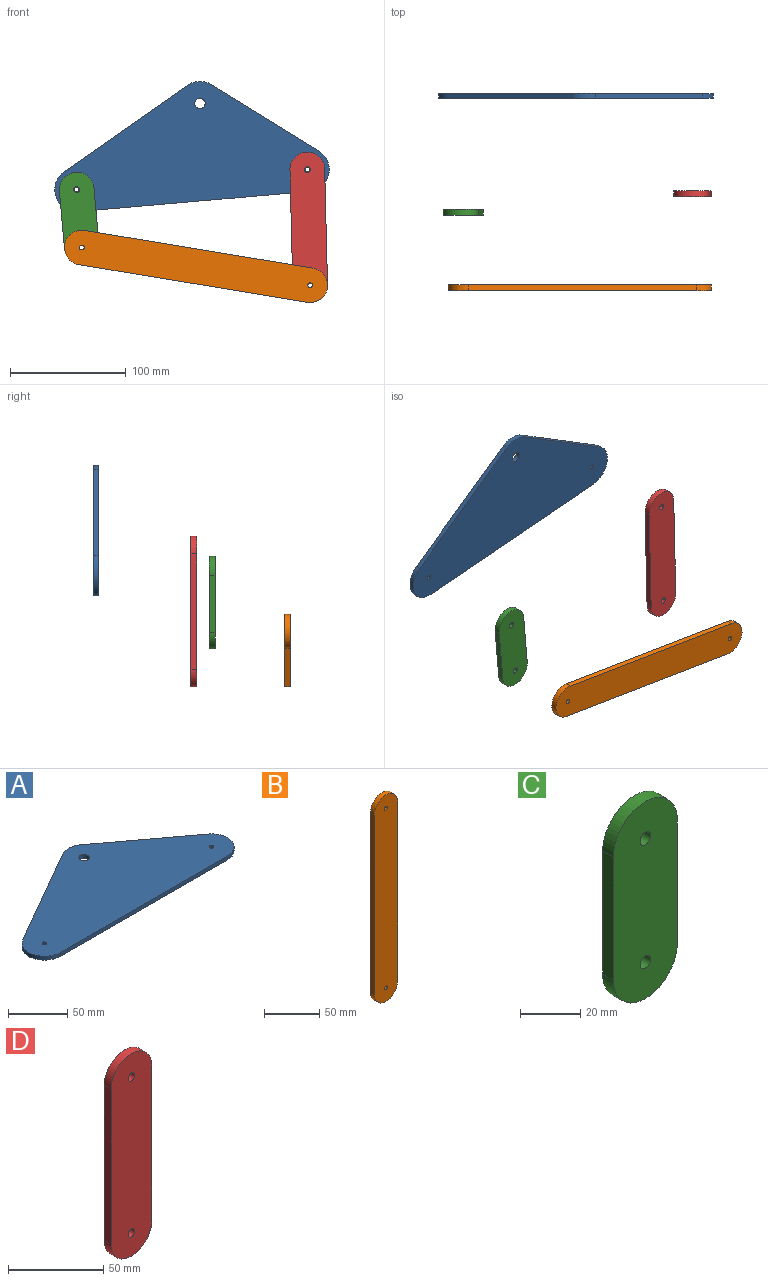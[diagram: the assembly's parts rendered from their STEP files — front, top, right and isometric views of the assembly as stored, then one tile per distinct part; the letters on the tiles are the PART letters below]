
ASSEMBLY  parts=4 mates=4
PART A: 11 faces, bbox 238x103x4 mm
  f0: plane 112.58x65mm, normal (-0.5,0.87,0), area 520mm2, adj f1,f8,f9,f10
  f1: cylinder r=19mm len=35.45mm, axis (0,0,-1), area 199mm2, adj f0,f2,f9,f10
  f2: plane 200x4mm, normal (0,-1,0), area 800mm2, adj f1,f3,f9,f10
  f3: cylinder r=19mm len=34.25mm, axis (0,0,-1), area 190.2mm2, adj f2,f4,f9,f10
  f4: plane 87.42x65mm, normal (0.6,0.8,0), area 435.7mm2, adj f3,f8,f9,f10
  f5: cylinder r=2mm len=4mm, axis (0,0,-1), area 50.3mm2, adj f9,f10
  f6: cylinder r=4.5mm len=9mm, axis (0,0,-1), area 113.1mm2, adj f9,f10
  f7: cylinder r=2mm len=4mm, axis (0,0,-1), area 50.3mm2, adj f9,f10
  f8: cylinder r=19mm len=20.84mm, axis (0,0,-1), area 88.4mm2, adj f0,f4,f9,f10
  f9: plane 238x103mm, normal (0,0,1), area 15885.1mm2, adj f0,f1,f2,f3,f4,f5,f6,f7
  f10: plane 238x103mm, normal (0,0,-1), area 15885.1mm2, adj f0,f1,f2,f3,f4,f5,f6,f7
PART B: 8 faces, bbox 30x5x230 mm
  f0: plane 200x5mm, normal (1,0,0), area 1000mm2, adj f1,f5,f6,f7
  f1: cylinder r=15mm len=30mm, axis (0,1,0), area 235.6mm2, adj f0,f2,f6,f7
  f2: plane 200x5mm, normal (-1,0,0), area 1000mm2, adj f1,f5,f6,f7
  f3: cylinder r=2mm len=5mm, axis (0,1,0), area 62.8mm2, adj f6,f7
  f4: cylinder r=2mm len=5mm, axis (0,1,0), area 62.8mm2, adj f6,f7
  f5: cylinder r=15mm len=30mm, axis (0,1,0), area 235.6mm2, adj f0,f2,f6,f7
  f6: plane 230x30mm, normal (0,-1,0), area 6681.7mm2, adj f0,f1,f2,f3,f4,f5
  f7: plane 230x30mm, normal (0,1,0), area 6681.7mm2, adj f0,f1,f2,f3,f4,f5
PART C: 8 faces, bbox 30x5x80 mm
  f0: plane 50x5mm, normal (-1,0,0), area 250mm2, adj f1,f4,f6,f7
  f1: cylinder r=15mm len=30mm, axis (0,1,0), area 235.6mm2, adj f0,f2,f6,f7
  f2: plane 50x5mm, normal (1,0,0), area 250mm2, adj f1,f4,f6,f7
  f3: cylinder r=2.5mm len=5mm, axis (0,1,0), area 78.5mm2, adj f6,f7
  f4: cylinder r=15mm len=30mm, axis (0,1,0), area 235.6mm2, adj f0,f2,f6,f7
  f5: cylinder r=2.5mm len=5mm, axis (0,1,0), area 78.5mm2, adj f6,f7
  f6: plane 80x30mm, normal (0,-1,0), area 2167.6mm2, adj f0,f1,f2,f3,f4,f5
  f7: plane 80x30mm, normal (0,1,0), area 2167.6mm2, adj f0,f1,f2,f3,f4,f5
PART D: 8 faces, bbox 30x5x130 mm
  f0: plane 100x5mm, normal (-1,0,0), area 500mm2, adj f1,f4,f6,f7
  f1: cylinder r=15mm len=30mm, axis (0,1,0), area 235.6mm2, adj f0,f2,f6,f7
  f2: plane 100x5mm, normal (1,0,0), area 500mm2, adj f1,f4,f6,f7
  f3: cylinder r=2.5mm len=5mm, axis (0,1,0), area 78.5mm2, adj f6,f7
  f4: cylinder r=15mm len=30mm, axis (0,1,0), area 235.6mm2, adj f0,f2,f6,f7
  f5: cylinder r=2.5mm len=5mm, axis (0,1,0), area 78.5mm2, adj f6,f7
  f6: plane 130x30mm, normal (0,-1,0), area 3667.6mm2, adj f0,f1,f2,f3,f4,f5
  f7: plane 130x30mm, normal (0,1,0), area 3667.6mm2, adj f0,f1,f2,f3,f4,f5
PLACE A rot(axis=(1,-0.04,0.04),90.1deg) t=(-272.71,107.2,220.88)mm
PLACE B rot(axis=(0,1,0),99.4deg) t=(-280.69,-57.8,188.17)mm
PLACE C rot(axis=(0,-1,0),5deg) t=(-281.98,7.2,154.82)mm
PLACE D rot(axis=(0,-1,0),1.4deg) t=(-85.63,23.2,122.98)mm
MATE cylindrical A.f1 <-> C.f4  axis (0,-1,0) through (-272.71,103.2,220.88)mm
MATE cylindrical B.f4 <-> C.f3  axis (0,1,0) through (-268.34,-57.8,170.92)mm
MATE cylindrical D.f3 <-> B.f1  axis (0,-1,0) through (-71.01,18.2,138.34)mm
MATE cylindrical A.f7 <-> D.f1  axis (0,-1,0) through (-73.47,103.2,238.31)mm
